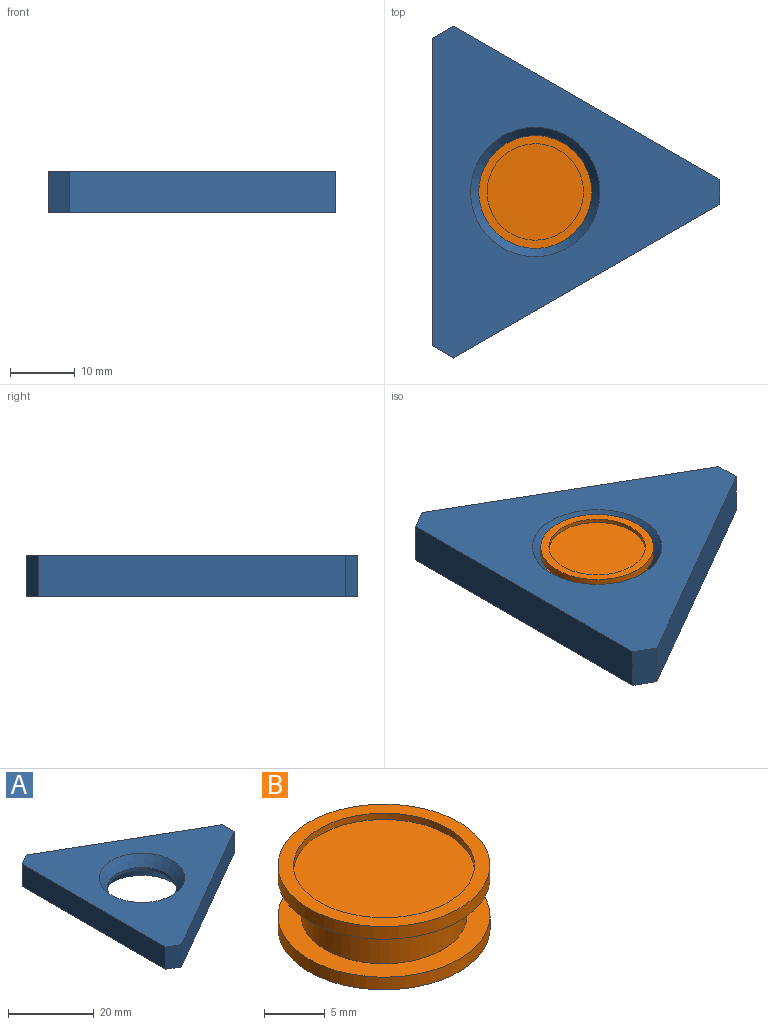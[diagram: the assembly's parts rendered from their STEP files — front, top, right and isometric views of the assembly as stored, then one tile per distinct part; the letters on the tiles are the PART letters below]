
ASSEMBLY  parts=2 mates=1
PART A: 11 faces, bbox 44.3x51.2x6.4 mm
  f0: plane 47.37x6.35mm, normal (-1,0,0), area 300.8mm2, adj f3,f4,f5,f6
  f1: plane 41.03x23.69mm, normal (0.5,-0.87,0), area 300.8mm2, adj f3,f4,f6,f7
  f2: plane 41.03x23.69mm, normal (0.5,0.87,0), area 300.8mm2, adj f3,f4,f5,f7
  f3: plane 51.18x44.33mm, normal (0,0,1), area 978mm2, adj f0,f1,f2,f5,f6,f7,f10
  f4: plane 51.18x44.33mm, normal (0,0,-1), area 978mm2, adj f0,f1,f2,f5,f6,f7,f9
  f5: plane 6.35x3.3mm, normal (-0.5,0.87,0), area 24.2mm2, adj f0,f2,f3,f4
  f6: plane 6.35x3.3mm, normal (-0.5,-0.87,0), area 24.2mm2, adj f0,f1,f3,f4
  f7: plane 6.35x3.81mm, normal (1,0,0), area 24.2mm2, adj f1,f2,f3,f4
  f8: cylinder r=8.06mm len=16.13mm, axis (0,0,-1), area 45mm2, adj f9,f10
  f9: cone r=9.98mm half-angle=35deg, axis (0,0,-1), area 188.9mm2, adj f4,f8
  f10: cone r=8.06mm half-angle=35deg, axis (0,0,1), area 188.9mm2, adj f3,f8
PART B: 11 faces, bbox 17.4x17.4x6.4 mm
  f0: cylinder r=6.79mm len=13.59mm, axis (0,0,-1), area 162.7mm2, adj f2,f5
  f1: cylinder r=8.7mm len=17.4mm, axis (0,0,-1), area 69.4mm2, adj f2,f3
  f2: plane 17.4x17.4mm, normal (0,0,1), area 92.7mm2, adj f0,f1
  f3: plane 17.4x17.4mm, normal (0,0,-1), area 64.4mm2, adj f1,f9
  f4: cylinder r=8.7mm len=17.4mm, axis (0,0,1), area 69.4mm2, adj f5,f6
  f5: plane 17.4x17.4mm, normal (0,0,-1), area 92.7mm2, adj f0,f4
  f6: plane 17.4x17.4mm, normal (0,0,1), area 64.4mm2, adj f4,f7
  f7: cylinder r=7.43mm len=14.86mm, axis (0,0,1), area 29.6mm2, adj f6,f8
  f8: plane 14.86x14.86mm, normal (0,0,1), area 173.4mm2, adj f7
  f9: cylinder r=7.43mm len=14.86mm, axis (0,0,-1), area 29.6mm2, adj f3,f10
  f10: plane 14.86x14.86mm, normal (0,0,-1), area 173.4mm2, adj f9
PLACE A t=(-13.78,-3.09,-1.32)mm
PLACE B t=(-13.78,-3.09,-1.32)mm
MATE fastened B.f0 <-> A.f8  axis (0,0,-1) through (-13.78,-3.09,1.86)mm
